# Revit family: 937200001_REJILLA PISO VANGUARDISTA
name_source: partatom
category: Plumbing Fixtures
units: mm (PartAtom-declared; Revit-internal decimal feet)

## family parameters
Always vertical = Yes
Cut with Voids When Loaded = No
OmniClass Number = 23.39.29.15
OmniClass Title = Waste Water Channels, Gullies, Gratings, Covers
Part Type = Normal
Room Calculation Point = No
Round Connector Dimension = Use Diameter
Shared = No
Work Plane-Based = No

## types (1)
- 937200001_REJILLA PISO VANGUARDISTA
    Creado por = IDD
    Description = Fabricada 100% en acero inoxidable, alta resistencia a la corrosión y cuenta con sistema anticucarachas y olores
    Dimensiónes generales de producto (H x W x L) = 54 x 99 x 99 mm. / 2,1 x 3,9 x 3,9 pulg
    Fecha de creación = 3/08/2020
    Material = Corona_Acero inoxidable
    Materiales = Acero inoxidable
    Peso bruto aproximado = 240gr. / 0,53Lb
    Peso neto aproximado = 210gr. / 0,46Lb
    REFERENCIAS DE PRODUCTO 1 = 937200001 REJILLA PISO VANGUAR 10X10CM 11/2 -3P
    REFERENCIAS DE PRODUCTO 2 = 937205551 REJ PISO VANGUAR 10X10 11/2 -3P M6 CP5
    REFERENCIAS DE PRODUCTO 3 = 937203331 REJILLA PISO VANGUARDISTA X 3
    Recubrimientos = No tóxico
    Resistente = Corrosión, pelado y decoloración por agua
    Sistema = Anticucarachas y olores
    Tipo de activo = Fijo
    URL = https://www.grival.com
    Uso = Doméstico

## geometry (parser evidence)
native form markers: Sweep x2
no freeform markers — native parametric forms only
